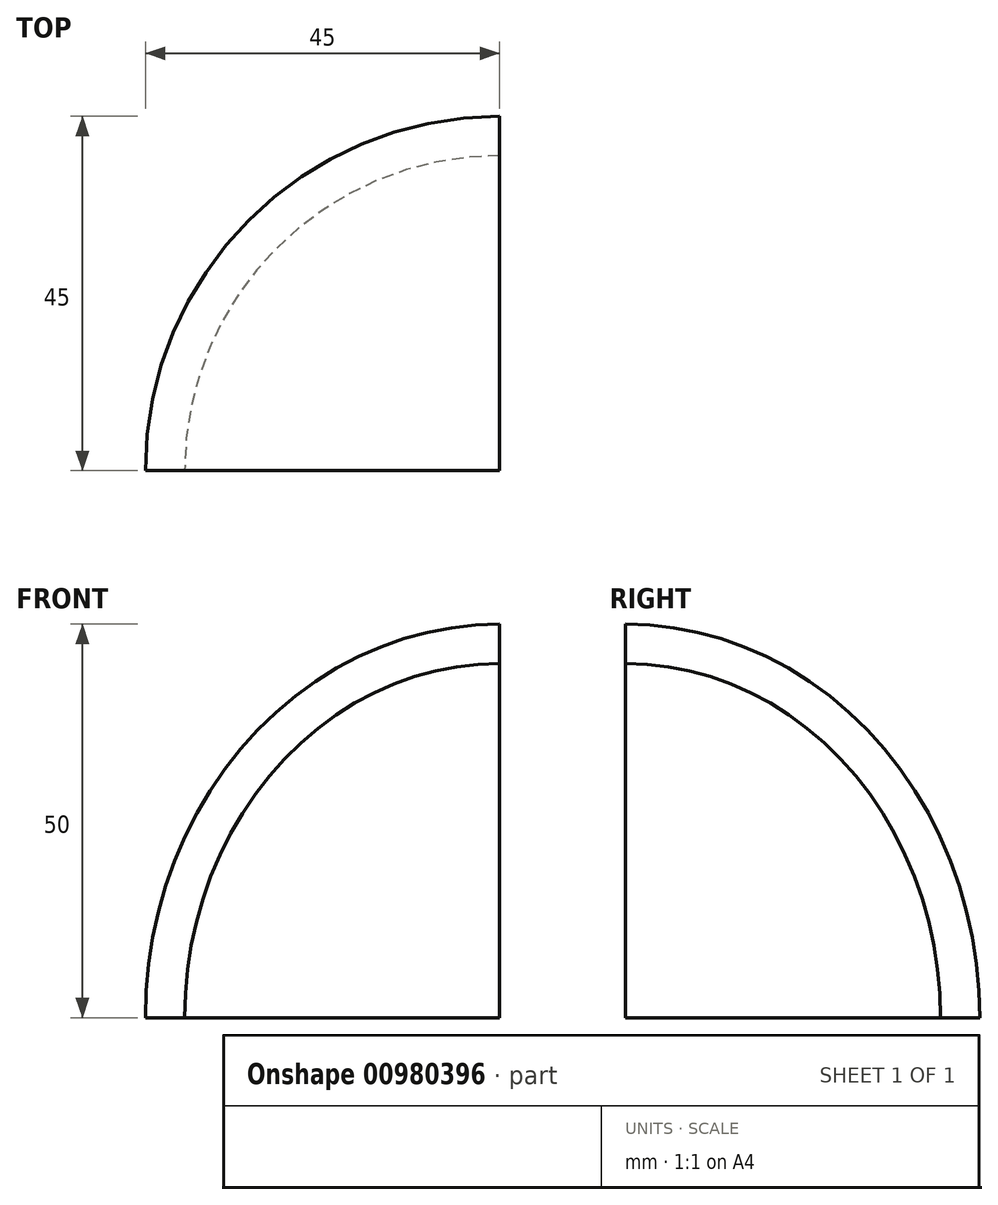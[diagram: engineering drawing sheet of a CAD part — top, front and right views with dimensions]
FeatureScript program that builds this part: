
annotation { "Feature Type Name" : "Feature", "Feature Type Description" : "" }
export const myFeature = defineFeature(function(context is Context, id is Id, definition is map)
    precondition{}
    {
        {
            var Q0;
            Q0=qCreatedBy(makeId("Front.planeOp"),FACE);
            var sketch = newSketch(context, id + "F0", { "sketchPlane" : qUnion([Q0])});
            skEllipticalArc(sketch, "E0", {});
            skLineSegment(sketch, "E1", {"start": v(0, 50) * mm, "end": v(0, 45) * mm});
            skLineSegment(sketch, "E2", {"start": v(-45, 0) * mm, "end": v(-40, 0) * mm});
            skPoint(sketch, "E3", {"position": v(0, 45) * mm});
            skPoint(sketch, "E4", {"position": v(-40, 0) * mm});
            skEllipticalArc(sketch, "E5", {});
            skLineSegment(sketch, "E6", {"start": v(0, 60.2) * mm, "end": v(0, 0) * mm});
            const initialGuessF0  = {"E0": [0, 0, 0, 1, 0.05, 0.045, 0, 1.5707963267948966], "E5": [0, 0, 0, 1, 0.045, 0.04, 0, 1.5707963267948966]};
            skSetInitialGuess(sketch, initialGuessF0);
            skSolve(sketch);
        }
        {
            var Q0;
            {var subQ0=sQuery(id+"F0.wireOp",EDGE,"E0");Q0=makeQuery(id+"F0.imprint","IMPRINT",FACE,{"disambiguationData":[TD([[makeQuery(id+"F0.imprint","IMPRINT",EDGE,{"derivedFrom":subQ0}),1.0]])]});}
            var Q1;
            Q1=sQuery(id+"F0.wireOp",EDGE,"E6");
            revolve(context, id + "F1", {"surfaceOperationType" : NewSurfaceOperationType.NEW, "entities" : qUnion([Q0]), "axis" : qUnion([Q1]), "revolveType" : RevolveType.ONE_DIRECTION, "angle" : 90 * degree});
        }
    });
